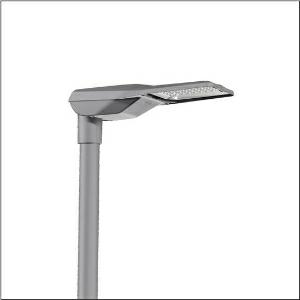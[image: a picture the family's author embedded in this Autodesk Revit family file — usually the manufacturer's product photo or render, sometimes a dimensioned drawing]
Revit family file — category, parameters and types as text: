
# Revit family: streetlight_sl_21_iq_mini___st0_8a_5xe2c41g08gb_95af
name_source: partatom
category: Lighting Fixtures
units: mm (PartAtom-declared; Revit-internal decimal feet)

## family parameters
Cut with Voids When Loaded = No
Host = Face
Light Source = No
Part Type = Normal
Room Calculation Point = No
Round Connector Dimension = Use Diameter
Shared = No

## types (1)
- --- (1 x LED, 5920 lm, 37.1 W, 4000K)
    Apparent Load = 37 VA
    CIE Flux Codes = 38 75 97 100 100
    Color Rendering = 70
    Color Temperature = 4000K
    Default Elevation = 1800 mm
    Description = Streetlight SL 21 iQ mini, mast luminaire, primary light control with lens, of PMMA, primary optical cover: cover, of toughened safety glass, transparent, light distribution: ST0.8a, light emission: direct distribution, primary light characteristic: asymmetric, installation type: post-top, side-entry, LED, High Power LED, rated luminous flux: 5.920lm, luminous efficacy: 160lm/W, light colour: 740, colour temperature: 4000K, control gear: iQ Street-Remote, control: Street-Remote, Auto-Match, Temp-Guard, Lumen-Switch, Night-Set, Smart-Wire, Light-Fading, Desk-Remote (wireless, voltage-free reading and setting of iQ features in the workshop via application-optimized NFC function/RFID function), optimised constant luminous flux control (CLO 2.0), pre-setting: linear dimming characteristic, mains connection: 220..240V, AC, 50/60Hz, start of lifetime: 37W, end of service life: 39W, reduction: 18W, luminaire housing, of diecast aluminium, powder-coated, Siteco® metallic grey (DB 702S), corrosivity category C5 mid according to DIN EN ISO 12944, please order mast flange separately, inclination adjustable: 0°, 5°, 10°, 15°, sealing non-destructively replaceable, multi-level sealing system, length: 628mm, width: 235mm, height: 110mm, mast flange for spigot size: 42mm (side-entry): 5XC10008XM4, 60/48mm (side-entry/post-top): 5XC10108XM2, 76/60mm (side-entry/post-top): 5XC10108XM1, mounting height: 4..8m, protection rating (complete): IP66, insulation class (complete): insulation class II (safety insulation), certification: CE, ENEC, ENEC+, VDE, impact resistance: IK10, permissible operating ambient temperature for outdoor applications: -40..+50°C, standard-compliant lighting for roads and squares, packaging unit: 1 piece

Light Distribution: ST0.8a
    Height = 110 mm
    Lamp = 1 x LED
    Lamp Light Flux = 5920 lm
    Lamp Power = 37.1 W
    Lamp count = 1
    Length = 625 mm
    Luminous efficacy = 160 lm/W
    Manufacturer = Siteco
    ModVariant = No
    Model = 5XE2C41G08GB
    Number of Poles = 1
    OnlyDefault = Yes
    Power Factor = 1
    Product Name = Streetlight SL 21 iQ mini | ST0.8a
    Product group = mast luminaire | pylon top
    ProductGroupID = 6100
    Protection Class = Protection class II
    Protection Degree = IP 66
    RLX_Detail_Level = 1
    RLX_Emergency_Light_Flux = 0 lm
    RLX_Emergency_Type = 0
    RLX_Emergency_Type_DB = No
    RlxData = <blob elided: 26369 chars, md5=8d35d0e7>
    Socket = socket
    Standby Power = 0 W
    System Light Flux = 5920 lm
    System Power = 37 W
    Type Comments = factory setting: luminous flux: 100 % | dim-lin: 254 | 385 mA
    Type Image = l_1003519.jpg
    URL = http://relux.com
    VarID = @adj_206903
    Voltage = 0 V
    Weight = 0.00 kg
    Width = 234 mm

## geometry (parser evidence)
native form markers: Blend x4, Sweep x13
no freeform markers — native parametric forms only
